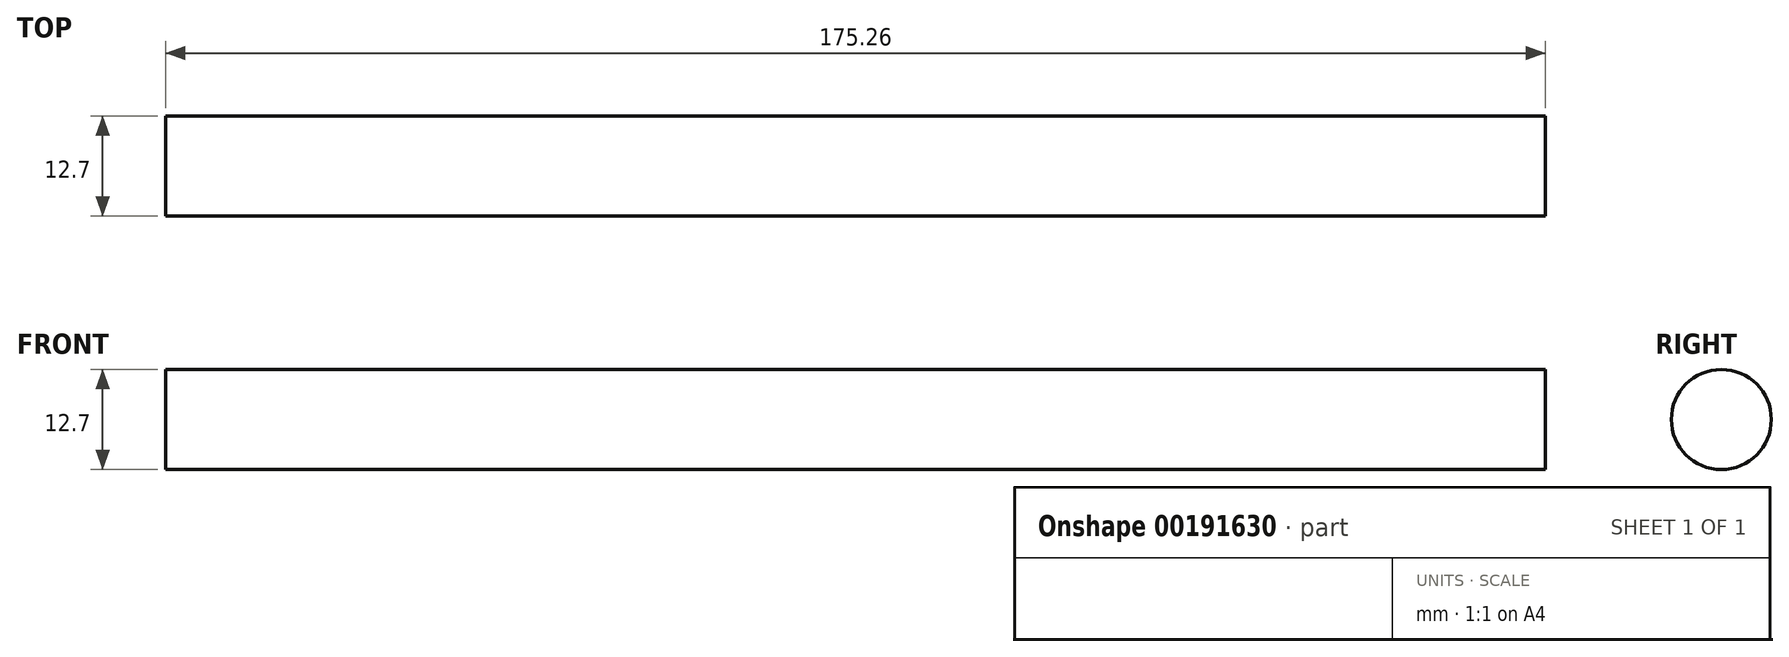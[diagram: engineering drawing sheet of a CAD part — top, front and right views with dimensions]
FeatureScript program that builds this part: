
annotation { "Feature Type Name" : "Feature", "Feature Type Description" : "" }
export const myFeature = defineFeature(function(context is Context, id is Id, definition is map)
    precondition{}
    {
        {
            var Q0;
            Q0=qCreatedBy(makeId("Right.planeOp"),FACE);
            var sketch = newSketch(context, id + "F0", { "sketchPlane" : qUnion([Q0])});
            skCircle(sketch, "E0", {"center": v(0, 0) * mm, "radius": 6.35 * mm});
            skSolve(sketch);
        }
        {
            var Q0;
            Q0=makeQuery(id+"F0.imprint","IMPRINT",FACE,{"disambiguationData":[TD([[makeQuery(id+"F0.imprint","IMPRINT",EDGE,{"derivedFrom":sQuery(id+"F0.wireOp",EDGE,"E0")}),1.0]])]});
            extrude(context, id + "F1", {"entities" : qUnion([Q0]), "depth" : 175.26 * mm});
        }
    });
